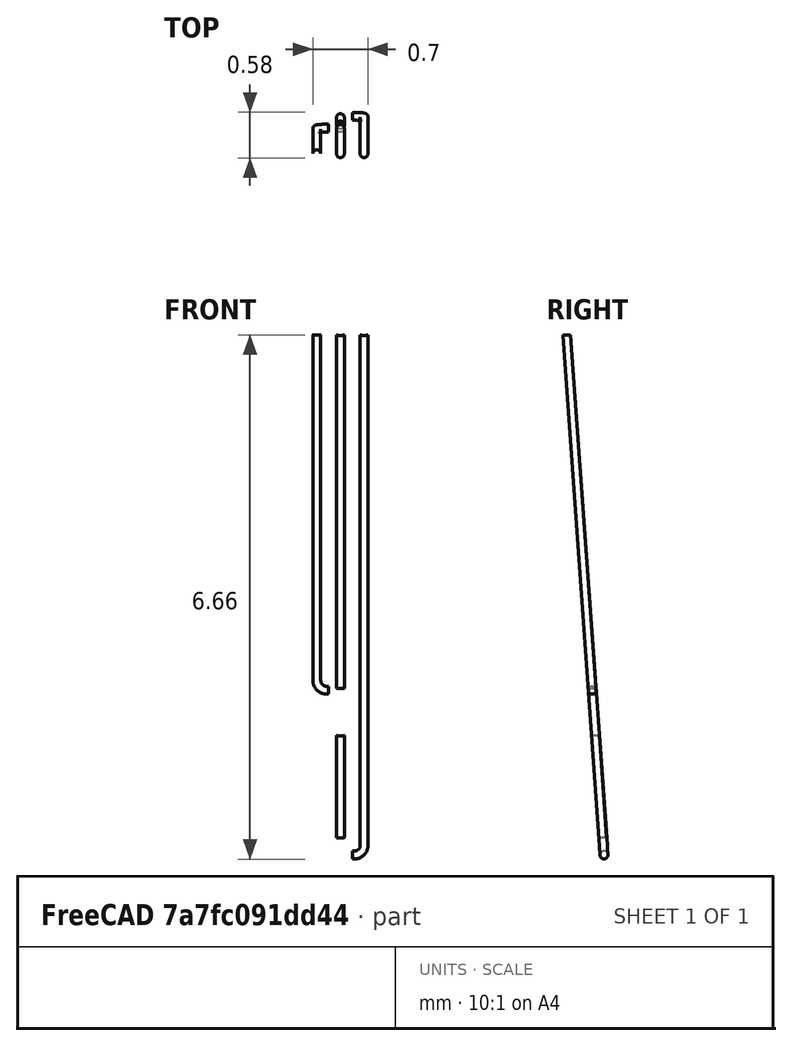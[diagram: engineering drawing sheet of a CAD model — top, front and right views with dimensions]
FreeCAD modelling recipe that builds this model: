
FCSTD DOCUMENT  (FreeCAD 0.16R6712 (Git))
Label: sepwires
License: All rights reserved
LicenseURL: http://en.wikipedia.org/wiki/All_rights_reserved
objects: Sketcher::SketchObject×4, Part::Sweep×2, Part::Cylinder×2, Part::MultiFuse×1, Mesh::Feature×1
note: 9 computed .brp shape members not serialized (recipe doc carries the construction recipe); baked Part::Feature solids carry a one-line shape summary decoded from their .brp

FEATURE [Sketcher::SketchObject] Sketch
  Placement = pos=(0,-2,0) rot=(1,0,0;1.5708rad)
  sketch-geometry (1):
    g0: Circle CenterX=0.3 CenterY=0 CenterZ=0 NormalX=0 NormalY=0 NormalZ=1 Radius=0.05
  constraints (3):
    c: PointOnObject(g0,g-1)
    c: Radius(g0) = 0.05
    c: DistanceX(g-2,g0) = 0.3
FEATURE [Sketcher::SketchObject] Sketch001
  sketch-geometry (3):
    g0: LineSegment StartX=0.3 StartY=-4 StartZ=0 EndX=0.3 EndY=2.5 EndZ=0
    g1: LineSegment StartX=0.177911 StartY=2.62209 StartZ=0 EndX=0.150112 EndY=2.62209 EndZ=0
    g2: ArcOfCircle CenterX=0.177911 CenterY=2.5 CenterZ=0 NormalX=0 NormalY=0 NormalZ=1 Radius=0.122089 StartAngle=0 EndAngle=1.5708
  constraints (7):
    c: Vertical(g0)
    c: Distance(g-1,g0) = 0.3
    c: DistanceY(g-1,g0) = -4
    c: Horizontal(g1)
    c: Tangent(g0,g2) = -1.5708
    c: Tangent(g1,g2) = -1.5708
    c: DistanceY(g-1,g2) = 2.5
FEATURE [Part::Sweep] Sweep
  Frenet = true
  Sections = -> [Sketch]
  Solid = true
  Spine = -> Sketch001 [Edge2,Edge1,Edge3]
  Transition = 1
FEATURE [Part::Cylinder] Cylinder
  Angle = 360
  Height = 4.5
  Placement = pos=(0,-4,0) rot=(-1,0,0;1.5708rad)
  Radius = 0.05
FEATURE [Part::Cylinder] Cylinder001
  Angle = 360
  Height = 1.3
  Placement = pos=(0,1.1,0) rot=(-1,0,0;1.5708rad)
  Radius = 0.05
FEATURE [Sketcher::SketchObject] Sketch002
  Placement = pos=(0,-2,0) rot=(1,0,0;1.5708rad)
  sketch-geometry (1):
    g0: Circle CenterX=0.3 CenterY=0 CenterZ=0 NormalX=0 NormalY=0 NormalZ=1 Radius=0.05
  constraints (3):
    c: PointOnObject(g0,g-1)
    c: Radius(g0) = 0.05
    c: DistanceX(g-2,g0) = 0.3
FEATURE [Sketcher::SketchObject] Sketch003
  sketch-geometry (3):
    g0: LineSegment StartX=0.3 StartY=-4 StartZ=0 EndX=0.3 EndY=0.4 EndZ=0
    g1: LineSegment StartX=0.177111 StartY=0.522889 StartZ=0 EndX=0.150112 EndY=0.522889 EndZ=0
    g2: ArcOfCircle CenterX=0.177111 CenterY=0.4 CenterZ=0 NormalX=0 NormalY=0 NormalZ=1 Radius=0.122889 StartAngle=0 EndAngle=1.5708
  constraints (7):
    c: Vertical(g0)
    c: Distance(g-1,g0) = 0.3
    c: DistanceY(g-1,g0) = -4
    c: Horizontal(g1)
    c: Tangent(g0,g2) = -1.5708
    c: Tangent(g1,g2) = -1.5708
    c: DistanceY(g-1,g2) = 0.4
FEATURE [Part::Sweep] Sweep001
  Frenet = true
  Placement = pos=(0,0,0) rot=(0,1,0;3.14159rad)
  Sections = -> [Sketch002]
  Solid = true
  Spine = -> Sketch003 [Edge2,Edge1,Edge3]
  Transition = 1
FEATURE [Part::MultiFuse] Fusion
  Placement = pos=(0,0,0) rot=(-1,0,0;1.49911rad)
  Shapes = -> [Cylinder,Cylinder001,Sweep,Sweep001]
FEATURE [Mesh::Feature] Mesh  label="Fusion (Meshed)"
